# Revit family: 39-HC_VRF_HCL_TOSHIBA_TCAC_MCY6HT_04-05
name_source: partatom
category: Mechanical Equipment
revit_build: Autodesk Revit 2017 (Build: 20160225_1515(x64)
units: mm (PartAtom-declared; Revit-internal decimal feet)

## family parameters
Always vertical = Yes
Cut with Voids When Loaded = No
OmniClass Number = 23.75.00.00
OmniClass Title = Climate Control (HVAC)
Part Type = Normal
Room Calculation Point = No
Round Connector Dimension = Use Diameter
Shared = No
Work Plane-Based = No

## types (2) — shared parameters
Article Description = Signle fan Side Blow VRF
Compressor detail - Motor output  (kW) = 3.75
Compressor detail - Type = Hermetic twin rotary compressor
Content Supplier URL = www.hcltech.com
Custom = No
Depth (mm) = 390 mm  [stored 1.27953 ft]
Description = Signle fan Side Blow VRF
EMCS = 4
ETIM Article Class = EC001213
Frequency (Hz) = 50
Height (mm) = 910 mm  [stored 2.98556 ft]
Hydronic Return Diameter (mm) = 16 mm
Hydronic Supply Diameter (mm) = 10 mm  [stored 0.0328084 ft]
IFCExportType = NOTDEFINED
IFCExportas = IfcPumpType
MEPcontent Class = HEATPUMP
MOCP (A) = 32.0
Manufacturer = Toshiba
Manufacturer URL = www.toshiba-aircon.co.uk
Operating range - Cooling (°C) = -5  -  46
Operating range - Heating (°C) = -20 - 15
Part load = 30-100%
Product Line = TCAC
Red = Colour RGB-250 000 000
Refrigerant Type = R410A
Sound pressure - Cooling (dB) = 54.0
Starting current (A) = Soft Start
URL = www.toshiba-aircon.co.uk
Voltage (V) = 220 / 230 / 240
Weight (Kg) = 100
White = Colour RGB-255 255 255
Width (mm) = 990 mm  [stored 3.24803 ft]

## per-type parameters (varying)
| type | Airflow (m3/h) | Capacities - Cooling (kW) | Capacities - Heating (kW) | MCA (A) | Power consumption-Cooling (Kw) | Power consumption-Heating (Kw) | Rated efficiency - EER / COP | Running current-Cooling (A) | Running current-Heating (A) | Sound pressure - Heating (dB) |
| MCY-MHP0406HT-E | 4020 | 12.1 | 12.5 | 26.5 | 3.24 | 2.83 | 3.73 / 4.42 | 14.4 / 13.8 / 13.2 | 13.4 / 12.8 / 12.3 | 57.0 |
| MCY-MHP0506HT-E | 4260 | 14.0
14 | 16.0 | 28.0 | 3.94 | 3.86 | 3.56 / 4.15 | 18.7 / 17.9 / 17.1 | 18.3 / 17.5 / 16.8 | 58.0 |

note: column(s) folded — value = type name in every type: Article Type, Manufacturer Art. No., Model

note: [stored X ft] marks values corroborated as IEEE doubles in the binary element streams (Revit-internal decimal feet)

## geometry (parser evidence)
native form markers: Sweep x7
no freeform markers — native parametric forms only
